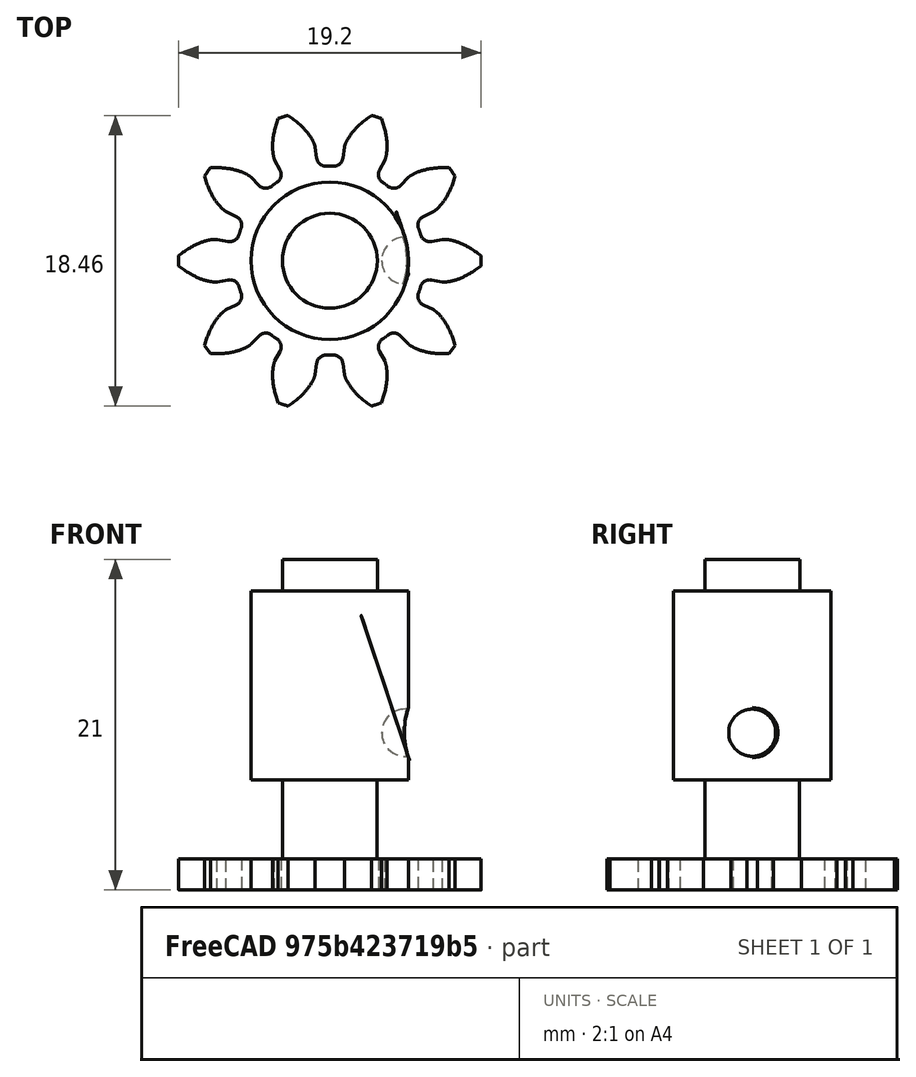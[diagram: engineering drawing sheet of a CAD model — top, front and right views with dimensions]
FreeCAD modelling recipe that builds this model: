
FCSTD DOCUMENT  (FreeCAD 0.19R24267 +148 (Git))
Label: AutomaticHopperShaft
License: All rights reserved
LicenseURL: http://en.wikipedia.org/wiki/All_rights_reserved
objects: Sketcher::SketchObject×2, Part::Cylinder×1, PartDesign::FeatureBase×1, PartDesign::Pad×1, PartDesign::SubtractiveSphere×1, PartDesign::Fillet×1, PartDesign::AdditiveCylinder×1, Part::Part2DObjectPython×1, PartDesign::Body×1, Part::Extrusion×1, Part::Compound×1
note: 16 computed .brp shape members not serialized (recipe doc carries the construction recipe); baked Part::Feature solids carry a one-line shape summary decoded from their .brp

FEATURE [Part::Cylinder] Cylinder
  Angle = 360
  AttacherType = Attacher::AttachEngine3D
  Height = 12
  Radius = 5
FEATURE [PartDesign::FeatureBase] BaseFeature
  BaseFeature = -> Cylinder
FEATURE [Sketcher::SketchObject] Sketch
  FullyConstrained = false
  MapMode = 5
  Placement = pos=(0,0,12) rot=(0,0,1;0rad)
  Support = -> [BaseFeature]
  sketch-geometry (1):
    g0: Circle CenterX=0 CenterY=0 CenterZ=0 NormalX=0 NormalY=0 NormalZ=1 AngleXU=0 Radius=3.01453
  constraints (1):
    c: Coincident(g0,g-1)
FEATURE [PartDesign::Pad] Pad
  BaseFeature = -> BaseFeature
  Direction = (1,1,1)
  Length = 2
  Length2 = 100
  Profile = -> Sketch
  Type = 0
FEATURE [Sketcher::SketchObject] Sketch001
  FullyConstrained = true
  MapMode = 5
  Placement = pos=(0,0,0) rot=(0.57735,0.57735,0.57735;2.0944rad)
  Support = -> [YZ_Plane]
FEATURE [PartDesign::SubtractiveSphere] Sphere
  Angle1 = -90
  Angle2 = 90
  Angle3 = 360
  AttacherType = Attacher::AttachEngine3D
  AttachmentOffset = pos=(4.8,0,-3) rot=(0,0,1;0rad)
  BaseFeature = -> Pad
  MapMode = 5
  Placement = pos=(4.8,0,3) rot=(1,0,0;3.14159rad)
  Radius = 1.5
  Support = -> [Pad]
FEATURE [PartDesign::Fillet] Fillet
  Base = -> Sphere [Edge6,Edge3,Edge2]
  BaseFeature = -> Sphere
  Placement = pos=(4.8,0,3) rot=(1,0,0;3.14159rad)
  Radius = 0.1
  SupportTransform = false
FEATURE [PartDesign::AdditiveCylinder] Cylinder001
  Angle = 360
  AttacherType = Attacher::AttachEngine3D
  AttachmentOffset = pos=(-4.8,0,0) rot=(0,0,1;0rad)
  BaseFeature = -> Fillet
  Height = 5
  MapMode = 5
  Placement = pos=(0,4e-16,0) rot=(1,0,0;3.14159rad)
  Radius = 3
  Support = -> [Fillet]
FEATURE [Part::Part2DObjectPython] InvoluteGear  # Draft 2D object (typed FeaturePython)
  ExternalGear = true
  HighPrecision = true
  Modules = 1.6
  NumberOfTeeth = 10
  PressureAngle = 25
FEATURE [PartDesign::Body] Body
  BaseFeature = -> Cylinder
  Group = -> [BaseFeature,Sketch,Pad,Sketch001,Sphere,Fillet,Cylinder001,InvoluteGear]
  Origin = -> Origin
  Tip = -> Cylinder001
FEATURE [Part::Extrusion] Extrude
  Base = -> InvoluteGear
  Dir = (0,0,1)
  DirMode = 2
  FaceMakerClass = Part::FaceMakerBullseye
  LengthFwd = 2
  LengthRev = 0
  Placement = pos=(0,0,-7) rot=(0,0,1;0rad)
  Solid = true
  Symmetric = false
FEATURE [Part::Compound] Compound
  Links = -> [Body,Extrude]
